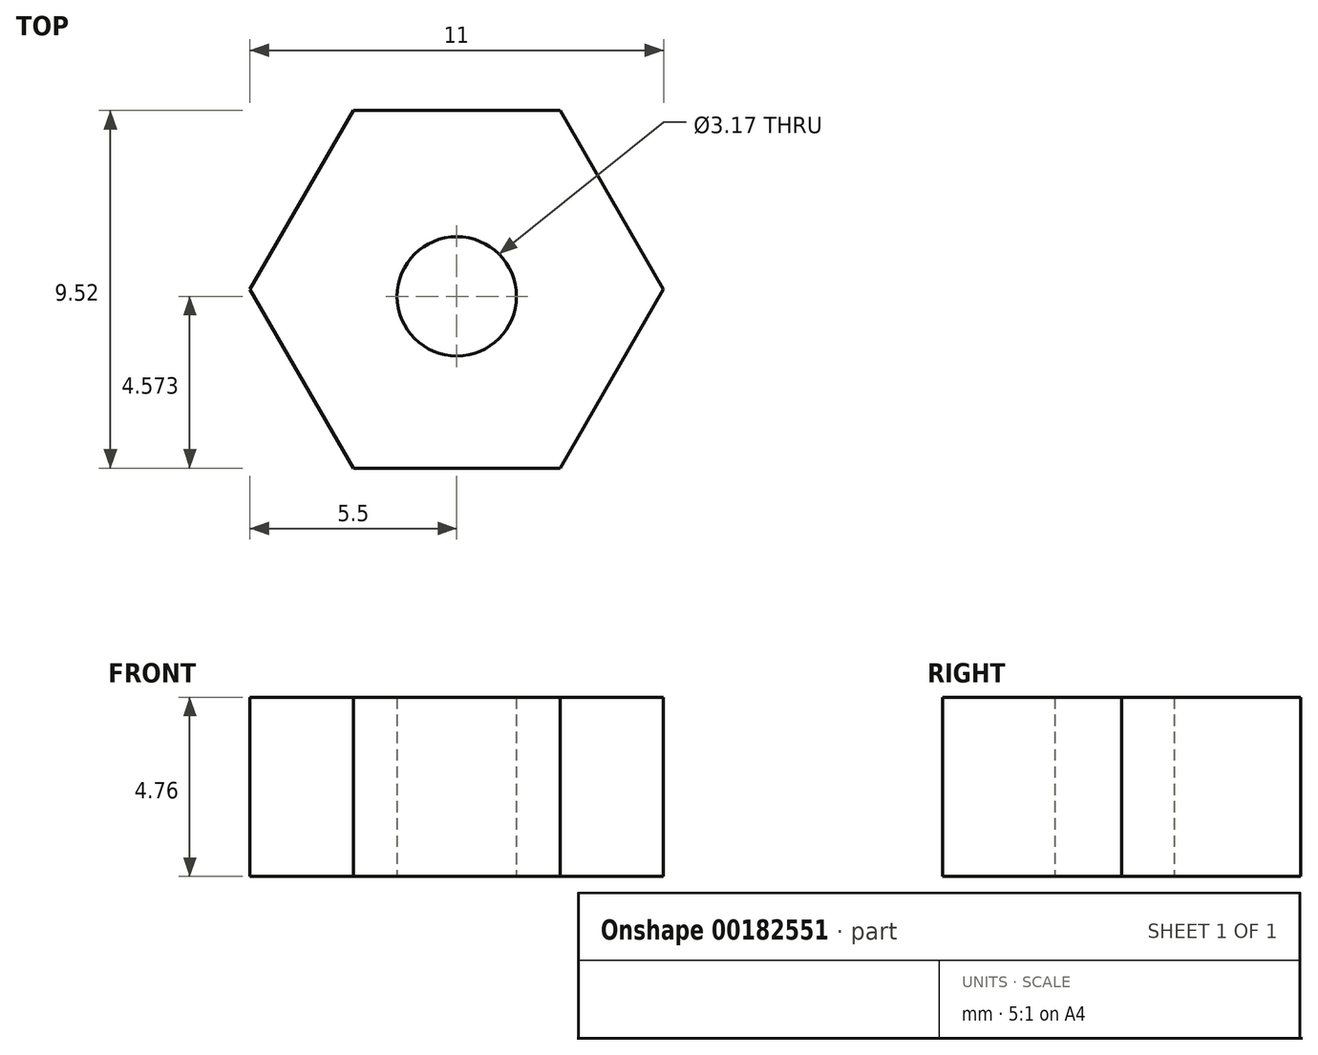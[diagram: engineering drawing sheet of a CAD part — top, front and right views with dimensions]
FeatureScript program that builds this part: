
annotation { "Feature Type Name" : "Feature", "Feature Type Description" : "" }
export const myFeature = defineFeature(function(context is Context, id is Id, definition is map)
    precondition{}
    {
        {
            var Q0;
            Q0=qCreatedBy(makeId("Top.planeOp"),FACE);
            var sketch = newSketch(context, id + "F0", { "sketchPlane" : qUnion([Q0])});
            skCircle(sketch, "E0.cCircle", {"center": v(0, 0) * mm, "radius": 4.76 * mm, "construction": true});
            skLineSegment(sketch, "E0.0", {"start": v(2.75, -4.76) * mm, "end": v(-2.75, -4.76) * mm});
            skLineSegment(sketch, "E0.1", {"start": v(-2.75, -4.76) * mm, "end": v(-5.5, 0) * mm});
            skLineSegment(sketch, "E0.2", {"start": v(-5.5, 0) * mm, "end": v(-2.75, 4.76) * mm});
            skLineSegment(sketch, "E0.3", {"start": v(-2.75, 4.76) * mm, "end": v(2.75, 4.76) * mm});
            skLineSegment(sketch, "E0.4", {"start": v(2.75, 4.76) * mm, "end": v(5.5, 0) * mm});
            skLineSegment(sketch, "E0.5", {"start": v(5.5, 0) * mm, "end": v(2.75, -4.76) * mm});
            skPoint(sketch, "E0.0.midPoint", {"position": v(0, -4.76) * mm});
            skCircle(sketch, "E1", {"center": v(0, -0.19) * mm, "radius": 1.59 * mm});
            skSolve(sketch);
        }
        {
            var Q0;
            Q0 = qSketchRegion(id + "F0", true);
            extrude(context, id + "F1", {"entities" : qUnion([Q0]), "depth" : 4.76 * mm});
        }
    });
